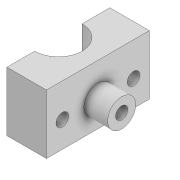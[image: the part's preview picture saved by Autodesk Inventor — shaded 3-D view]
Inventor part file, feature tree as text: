
AUTODESK INVENTOR PART (.ipt)
format: ipt  version: 2022 (Build 260153000, 153)  size: 137,216 bytes
history: native  units: mm
features: extrude x5, sketch x4, projected_geometry x1
ambient origin geometry x8: Origin, YZ Plane, XZ Plane, XY Plane, X Axis, Y Axis, Z Axis, Center Point
bodies: Solid1 (feature_tree)
feature tree (10):
  extrude  "Extrusion1"  Depth=10.0mm
  extrude  "Extrusion2"  Depth=10.0mm
  sketch  "Sketch3"  dims[d4=13.0mm d5=15.0mm d6=0.0mm]
  extrude  "Extrusion3"  Depth=15.0mm TaperAngle=0.0deg
  extrude  "Extrusion4"  Depth=6.0mm
  extrude  "Extrusion5"  Depth=6.0mm
  sketch  "Sketch1"  dims[d0=12.0mm d1=10.0mm]
  sketch  "Sketch2"  dims[d2=10.0mm d3=13.0mm]
  projected_geometry  "Projected Loop1"
  sketch  "Sketch5"  dims[d7=3.1mm d8=6.5mm d11=13.0mm d13=55.0mm d14=0.0mm d16=2.0mm d17=6.0mm d18=0.0mm d21=3.2mm d22=3.2mm d23=4.0mm d24=4.0mm d27=100.0mm d28=0.0mm d29=100.0mm d30=0.0mm]
